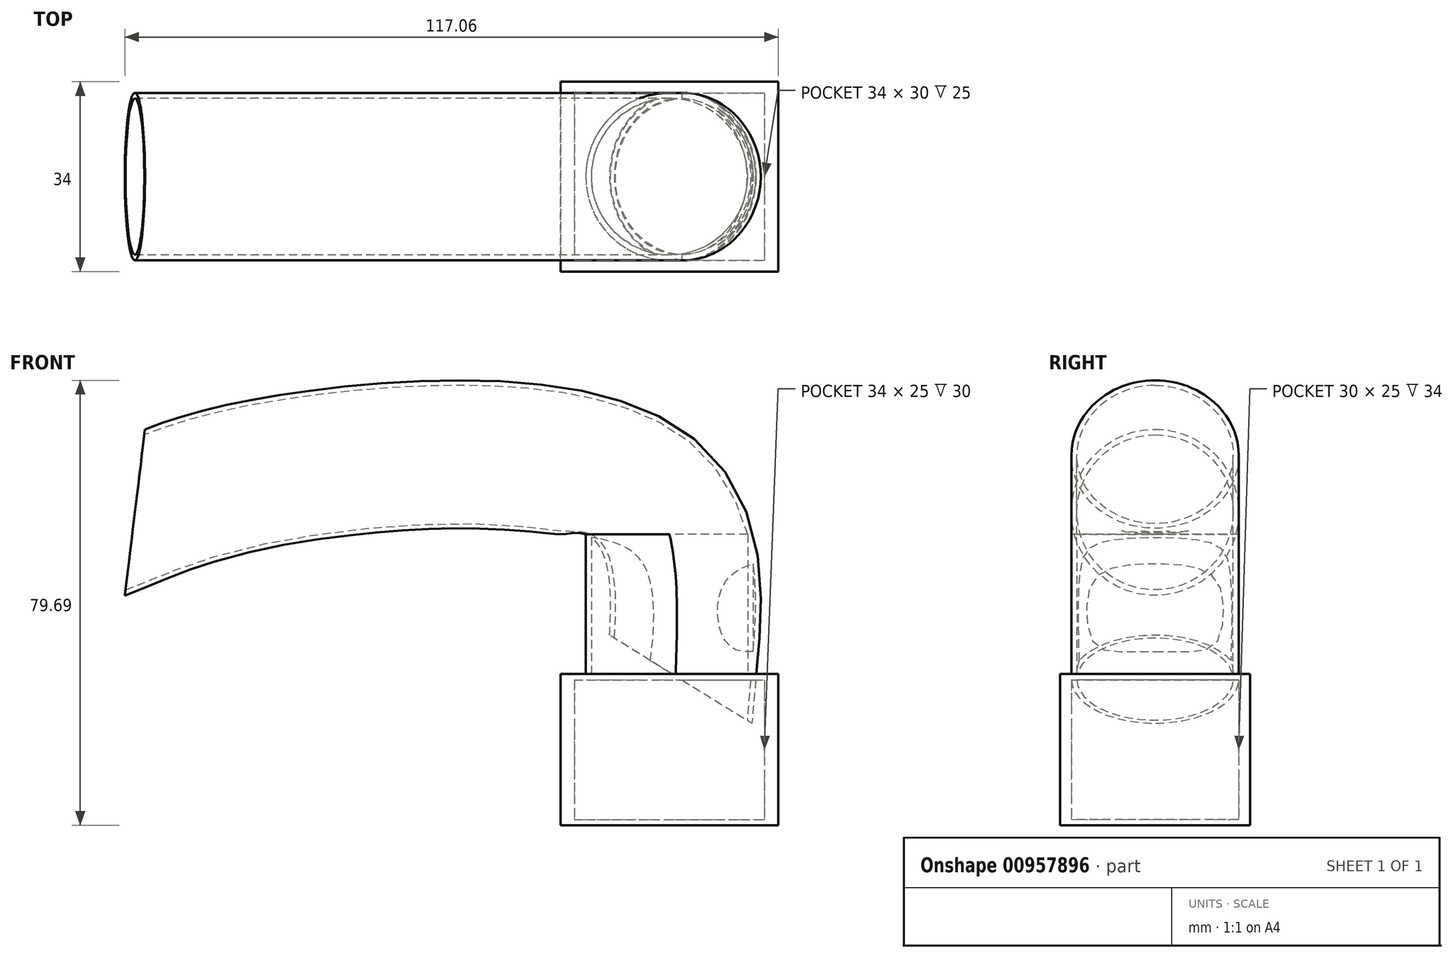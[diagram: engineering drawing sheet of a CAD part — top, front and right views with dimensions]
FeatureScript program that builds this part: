
annotation { "Feature Type Name" : "Feature", "Feature Type Description" : "" }
export const myFeature = defineFeature(function(context is Context, id is Id, definition is map)
    precondition{}
    {
        {
            var Q0;
            Q0=qCreatedBy(makeId("Top.planeOp"),FACE);
            var sketch = newSketch(context, id + "F0", { "sketchPlane" : qUnion([Q0])});
            skLineSegment(sketch, "E0.bottom", {"start": v(-19.5, 17) * mm, "end": v(19.5, 17) * mm});
            skLineSegment(sketch, "E0.top", {"start": v(-19.5, -17) * mm, "end": v(19.5, -17) * mm});
            skLineSegment(sketch, "E0.left", {"start": v(-19.5, 17) * mm, "end": v(-19.5, -17) * mm});
            skLineSegment(sketch, "E0.right", {"start": v(19.5, 17) * mm, "end": v(19.5, -17) * mm});
            skPoint(sketch, "E0.middle", {"position": v(0, 0) * mm});
            skLineSegment(sketch, "E1.bottom", {"start": v(-17, 15) * mm, "end": v(17, 15) * mm});
            skLineSegment(sketch, "E1.top", {"start": v(-17, -15) * mm, "end": v(17, -15) * mm});
            skLineSegment(sketch, "E1.left", {"start": v(-17, 15) * mm, "end": v(-17, -15) * mm});
            skLineSegment(sketch, "E1.right", {"start": v(17, 15) * mm, "end": v(17, -15) * mm});
            skSolve(sketch);
        }
        {
            var Q0;
            Q0 = qSketchRegion(id + "F0", true);
            extrude(context, id + "F1", {"entities" : qUnion([Q0]), "depth" : 25 * mm, "offsetDistance" : 25 * mm});
        }
        {
            var Q0;
            Q0=qCreatedBy(makeId("Top.planeOp"),FACE);
            var sketch = newSketch(context, id + "F2", { "sketchPlane" : qUnion([Q0])});
            skLineSegment(sketch, "E2.bottom", {"start": v(-19.5, -17) * mm, "end": v(19.5, -17) * mm});
            skLineSegment(sketch, "E2.top", {"start": v(-19.5, 17) * mm, "end": v(19.5, 17) * mm});
            skLineSegment(sketch, "E2.left", {"start": v(-19.5, -17) * mm, "end": v(-19.5, 17) * mm});
            skLineSegment(sketch, "E2.right", {"start": v(19.5, -17) * mm, "end": v(19.5, 17) * mm});
            skPoint(sketch, "E2.middle", {"position": v(0, 0) * mm});
            skSolve(sketch);
        }
        {
            var Q0;
            Q0 = qSketchRegion(id + "F2", true);
            extrude(context, id + "F3", {"entities" : qUnion([Q0]), "operationType" : NewBodyOperationType.ADD, "oppositeDirection" : true, "depth" : 1 * mm, "offsetDistance" : 25 * mm});
        }
        {
            var Q0;
            Q0=makeQuery(id+"F1.opExtrude","CAP_FACE",FACE,{"disambiguationData":[OSD([sQuery(id+"F0.wireOp",EDGE,"E0.bottom"),sQuery(id+"F0.wireOp",EDGE,"E0.top"),sQuery(id+"F0.wireOp",EDGE,"E0.left"),sQuery(id+"F0.wireOp",EDGE,"E0.right"),sQuery(id+"F0.wireOp",EDGE,"E1.bottom"),sQuery(id+"F0.wireOp",EDGE,"E1.top"),sQuery(id+"F0.wireOp",EDGE,"E1.left"),sQuery(id+"F0.wireOp",EDGE,"E1.right")])],"isStart":false});
            var sketch = newSketch(context, id + "F4", { "sketchPlane" : qUnion([Q0])});
            skLineSegment(sketch, "E3.bottom", {"start": v(-19.5, 17) * mm, "end": v(19.5, 17) * mm});
            skLineSegment(sketch, "E3.top", {"start": v(-19.5, -17) * mm, "end": v(19.5, -17) * mm});
            skLineSegment(sketch, "E3.left", {"start": v(-19.5, 17) * mm, "end": v(-19.5, -17) * mm});
            skLineSegment(sketch, "E3.right", {"start": v(19.5, 17) * mm, "end": v(19.5, -17) * mm});
            skPoint(sketch, "E3.middle", {"position": v(0, 0) * mm});
            skSolve(sketch);
        }
        {
            var Q0;
            Q0 = qSketchRegion(id + "F4", true);
            extrude(context, id + "F5", {"entities" : qUnion([Q0]), "operationType" : NewBodyOperationType.ADD, "depth" : 1.1 * mm, "offsetDistance" : 25 * mm});
        }
        {
            var Q0;
            Q0=makeQuery(id+"F5.opExtrude","CAP_FACE",FACE,{"disambiguationData":[OSD([sQuery(id+"F4.wireOp",EDGE,"E3.bottom"),sQuery(id+"F4.wireOp",EDGE,"E3.top"),sQuery(id+"F4.wireOp",EDGE,"E3.left"),sQuery(id+"F4.wireOp",EDGE,"E3.right")])],"isStart":false});
            var sketch = newSketch(context, id + "F6", { "sketchPlane" : qUnion([Q0])});
            skCircle(sketch, "E4", {"center": v(0, 0) * mm, "radius": 15 * mm});
            skCircle(sketch, "E5", {"center": v(0, 0) * mm, "radius": 14 * mm});
            skSolve(sketch);
        }
        {
            var Q0;
            Q0 = qSketchRegion(id + "F6", true);
            extrude(context, id + "F7", {"entities" : qUnion([Q0]), "operationType" : NewBodyOperationType.ADD, "depth" : 25 * mm, "offsetDistance" : 25 * mm});
        }
        {
            var Q0;
            Q0=qCreatedBy(makeId("Front.planeOp"),FACE);
            var sketch = newSketch(context, id + "F8", { "sketchPlane" : qUnion([Q0])});
            skFitSpline(sketch, "E6", {"points": [v(0, 26.39) * mm, v(-7.06, 56.59) * mm, v(-68.76, 60.48) * mm, v(-96.04, 52.69) * mm], "startDerivative": vector(7.7, 120.23) * mm, "endDerivative": vector(-76.77, -29.6) * mm});
            skSolve(sketch);
        }
        {
            var Q0;
            Q0=makeQuery(id+"F7.opExtrude","CAP_FACE",FACE,{"disambiguationData":[OSD([sQuery(id+"F6.wireOp",EDGE,"E4"),sQuery(id+"F6.wireOp",EDGE,"E5")])],"isStart":false});
            var Q1;
            Q1=sQuery(id+"F8.wireOp",EDGE,"E6");
            sweep(context, id + "F9", {"operationType" : NewBodyOperationType.ADD, "profiles" : qUnion([Q0]), "path" : qUnion([Q1])});
        }
    });
